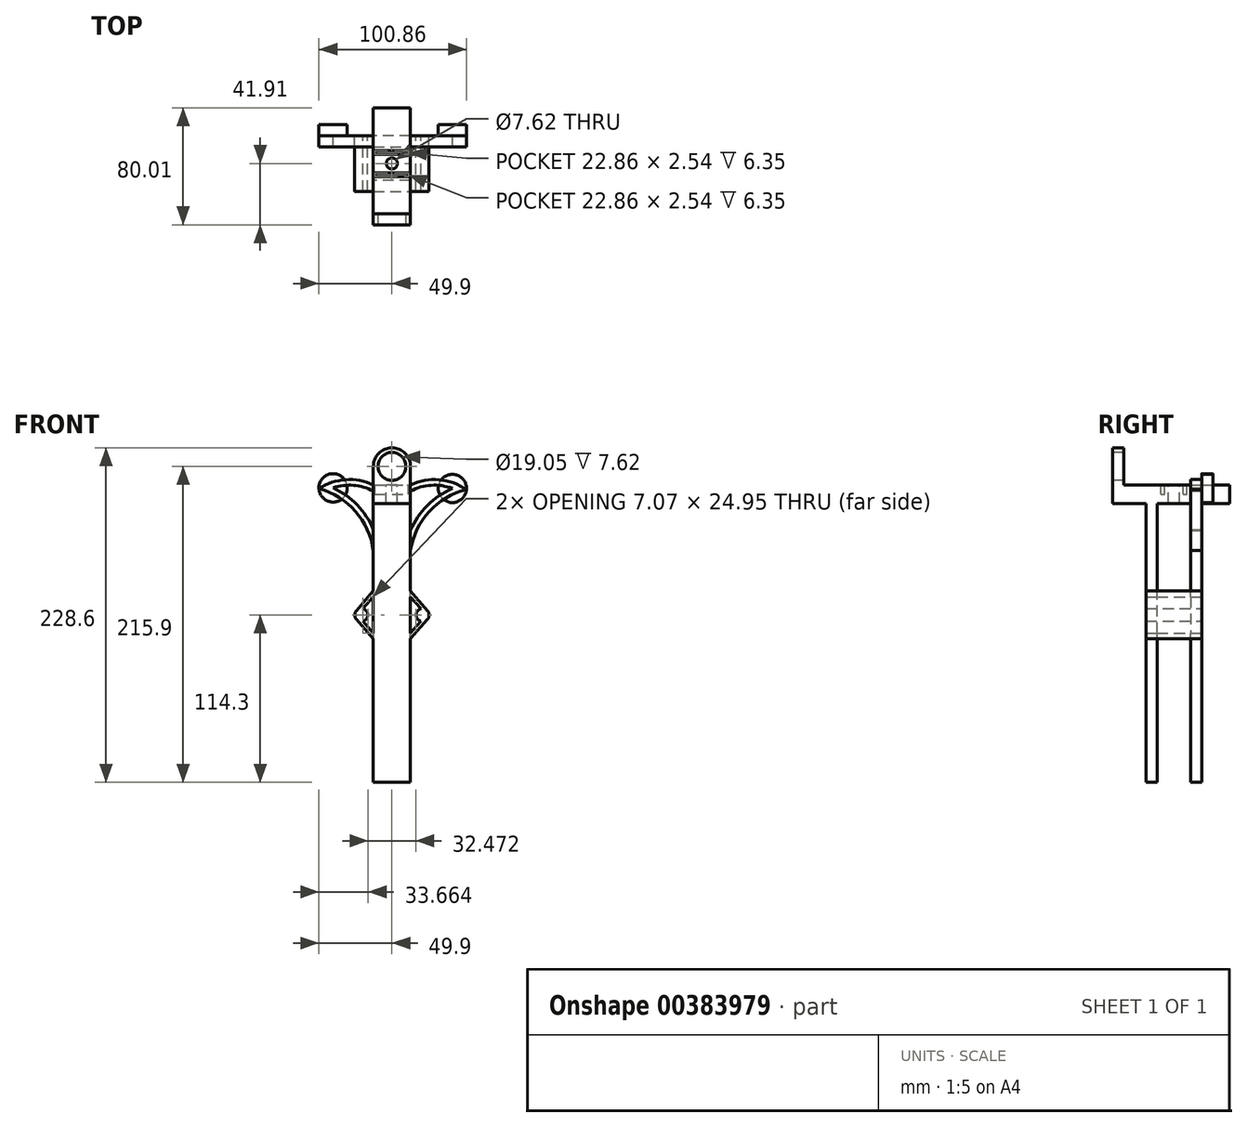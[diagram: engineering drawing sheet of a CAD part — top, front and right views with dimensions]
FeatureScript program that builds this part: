
annotation { "Feature Type Name" : "Feature", "Feature Type Description" : "" }
export const myFeature = defineFeature(function(context is Context, id is Id, definition is map)
    precondition{}
    {
        {
            var Q0;
            Q0=qCreatedBy(makeId("Front.planeOp"),FACE);
            var sketch = newSketch(context, id + "F0", { "sketchPlane" : qUnion([Q0])});
            skLineSegment(sketch, "E0", {"start": v(0, -63.5) * mm, "end": v(0, 139.7) * mm});
            skLineSegment(sketch, "E1", {"start": v(0, 139.7) * mm, "end": v(12.7, 139.7) * mm});
            skLineSegment(sketch, "E2", {"start": v(0, 139.7) * mm, "end": v(-12.7, 139.7) * mm});
            skLineSegment(sketch, "E3", {"start": v(-12.7, 139.7) * mm, "end": v(-12.7, -63.5) * mm});
            skLineSegment(sketch, "E4", {"start": v(-12.7, -63.5) * mm, "end": v(12.7, -63.5) * mm});
            skLineSegment(sketch, "E5", {"start": v(12.7, -63.5) * mm, "end": v(12.7, 139.7) * mm});
            skLineSegment(sketch, "E6", {"start": v(-25.4, 50.8) * mm, "end": v(25.4, 50.8) * mm});
            skArc(sketch, "E7", {"start": v(-24.32, 53.7) * mm, "mid": v(-25.4, 50.8) * mm, "end": v(-24.32, 47.9) * mm});
            skArc(sketch, "E8", {"start": v(24.32, 47.9) * mm, "mid": v(25.4, 50.8) * mm, "end": v(24.32, 53.7) * mm});
            skLineSegment(sketch, "E9", {"start": v(-24.32, 53.7) * mm, "end": v(-12.7, 67.16) * mm});
            skLineSegment(sketch, "E10", {"start": v(-24.32, 47.9) * mm, "end": v(-12.7, 34.44) * mm});
            skLineSegment(sketch, "E11", {"start": v(12.7, 67.16) * mm, "end": v(24.32, 53.7) * mm});
            skLineSegment(sketch, "E12", {"start": v(12.7, 34.44) * mm, "end": v(24.32, 47.9) * mm});
            skLineSegment(sketch, "E13.0", {"start": v(-19.77, 46.52) * mm, "end": v(-12.7, 38.32) * mm});
            skLineSegment(sketch, "E14.0", {"start": v(12.7, 38.32) * mm, "end": v(19.77, 46.52) * mm});
            skLineSegment(sketch, "E15.0", {"start": v(-19.77, 55.08) * mm, "end": v(-12.7, 63.28) * mm});
            skLineSegment(sketch, "E16.0", {"start": v(12.7, 63.28) * mm, "end": v(19.77, 55.08) * mm});
            skArc(sketch, "E17.trimOffspring", {"start": v(-19.77, 46.52) * mm, "mid": v(-16.51, 50.8) * mm, "end": v(-19.77, 55.08) * mm});
            skArc(sketch, "E18.trimOffspring", {"start": v(19.77, 55.08) * mm, "mid": v(16.5, 50.8) * mm, "end": v(19.77, 46.52) * mm});
            skPoint(sketch, "E19.orphan", {"position": v(25.4, 52.45) * mm});
            skSolve(sketch);
        }
        {
            var Q0;
            Q0 = qSketchRegion(id + "F0", true);
            extrude(context, id + "F1", {"entities" : qUnion([Q0]), "endBound" : BoundingType.SYMMETRIC, "depth" : 38.1 * mm});
        }
        {
            var Q0;
            Q0=makeQuery(id+"F1.opExtrude","SWEPT_FACE",FACE,{"disambiguationData":[OSD([sQuery(id+"F0.wireOp",EDGE,"E1"),sQuery(id+"F0.wireOp",EDGE,"E2")])]});
            var Q1;
            Q1=makeQuery(id+"F1.opExtrude","SWEPT_FACE",FACE,{"disambiguationData":[OSD([sQuery(id+"F0.wireOp",EDGE,"E11")])]});
            var Q2;
            {var subQ0=sQuery(id+"F0.wireOp",EDGE,"E5");Q2=makeQuery(id+"F1.opExtrude","SWEPT_FACE",FACE,{"disambiguationData":[OSD([subQ0]),TDD([makeQuery(id+"F0.imprint","IMPRINT",EDGE,{"disambiguationData":[TD([[makeQuery(id+"F0.imprint","INTERSECT",VERTEX,{"derivedFrom":[sQuery(id+"F0.wireOp",EDGE,"E1"),subQ0]}),1.0]])],"derivedFrom":subQ0})])]});}
            var Q3;
            {var subQ0=sQuery(id+"F0.wireOp",EDGE,"E5");Q3=makeQuery(id+"F1.opExtrude","SWEPT_FACE",FACE,{"disambiguationData":[OSD([subQ0]),TDD([makeQuery(id+"F0.imprint","IMPRINT",EDGE,{"disambiguationData":[TD([[makeQuery(id+"F0.imprint","INTERSECT",VERTEX,{"derivedFrom":[subQ0,sQuery(id+"F0.wireOp",EDGE,"E14.0")]}),-1.0]])],"derivedFrom":subQ0}),makeQuery(id+"F0.imprint","IMPRINT",EDGE,{"disambiguationData":[TD([[makeQuery(id+"F0.imprint","INTERSECT",VERTEX,{"derivedFrom":[subQ0,sQuery(id+"F0.wireOp",EDGE,"E16.0")]}),1.0]])],"derivedFrom":subQ0})])]});}
            var Q4;
            Q4=makeQuery(id+"F1.opExtrude","SWEPT_FACE",FACE,{"disambiguationData":[OSD([sQuery(id+"F0.wireOp",EDGE,"E12")])]});
            var Q5;
            {var subQ0=sQuery(id+"F0.wireOp",EDGE,"E5");Q5=makeQuery(id+"F1.opExtrude","SWEPT_FACE",FACE,{"disambiguationData":[OSD([subQ0]),TDD([makeQuery(id+"F0.imprint","IMPRINT",EDGE,{"disambiguationData":[TD([[makeQuery(id+"F0.imprint","INTERSECT",VERTEX,{"derivedFrom":[sQuery(id+"F0.wireOp",EDGE,"E4"),subQ0]}),-1.0]])],"derivedFrom":subQ0})])]});}
            var Q6;
            Q6=makeQuery(id+"F1.opExtrude","SWEPT_FACE",FACE,{"disambiguationData":[OSD([sQuery(id+"F0.wireOp",EDGE,"E4")])]});
            var Q7;
            {var subQ0=sQuery(id+"F0.wireOp",EDGE,"E3");Q7=makeQuery(id+"F1.opExtrude","SWEPT_FACE",FACE,{"disambiguationData":[OSD([subQ0]),TDD([makeQuery(id+"F0.imprint","IMPRINT",EDGE,{"disambiguationData":[TD([[makeQuery(id+"F0.imprint","INTERSECT",VERTEX,{"derivedFrom":[subQ0,sQuery(id+"F0.wireOp",EDGE,"E4")]}),1.0]])],"derivedFrom":subQ0})])]});}
            var Q8;
            Q8=makeQuery(id+"F1.opExtrude","SWEPT_FACE",FACE,{"disambiguationData":[OSD([sQuery(id+"F0.wireOp",EDGE,"E10")])]});
            var Q9;
            Q9=makeQuery(id+"F1.opExtrude","SWEPT_FACE",FACE,{"disambiguationData":[OSD([sQuery(id+"F0.wireOp",EDGE,"E9")])]});
            var Q10;
            {var subQ0=sQuery(id+"F0.wireOp",EDGE,"E3");Q10=makeQuery(id+"F1.opExtrude","SWEPT_FACE",FACE,{"disambiguationData":[OSD([subQ0]),TDD([makeQuery(id+"F0.imprint","IMPRINT",EDGE,{"disambiguationData":[TD([[makeQuery(id+"F0.imprint","INTERSECT",VERTEX,{"derivedFrom":[sQuery(id+"F0.wireOp",EDGE,"E2"),subQ0]}),-1.0]])],"derivedFrom":subQ0})])]});}
            var Q11;
            {var subQ0=sQuery(id+"F0.wireOp",EDGE,"E3");Q11=makeQuery(id+"F1.opExtrude","SWEPT_FACE",FACE,{"disambiguationData":[OSD([subQ0]),TDD([makeQuery(id+"F0.imprint","IMPRINT",EDGE,{"disambiguationData":[TD([[makeQuery(id+"F0.imprint","INTERSECT",VERTEX,{"derivedFrom":[subQ0,sQuery(id+"F0.wireOp",EDGE,"E15.0")]}),-1.0]])],"derivedFrom":subQ0}),makeQuery(id+"F0.imprint","IMPRINT",EDGE,{"disambiguationData":[TD([[makeQuery(id+"F0.imprint","INTERSECT",VERTEX,{"derivedFrom":[subQ0,sQuery(id+"F0.wireOp",EDGE,"E13.0")]}),1.0]])],"derivedFrom":subQ0})])]});}
            var Q12;
            Q12=makeQuery(id+"F1.opExtrude","SWEPT_BODY",BODY,{"disambiguationData":[OSD([sQuery(id+"F0.wireOp",EDGE,"E1"),sQuery(id+"F0.wireOp",EDGE,"E2"),sQuery(id+"F0.wireOp",EDGE,"E3"),sQuery(id+"F0.wireOp",EDGE,"E4"),sQuery(id+"F0.wireOp",EDGE,"E5"),sQuery(id+"F0.wireOp",EDGE,"E7"),sQuery(id+"F0.wireOp",EDGE,"E8"),sQuery(id+"F0.wireOp",EDGE,"E9"),sQuery(id+"F0.wireOp",EDGE,"E10"),sQuery(id+"F0.wireOp",EDGE,"E11"),sQuery(id+"F0.wireOp",EDGE,"E12"),sQuery(id+"F0.wireOp",EDGE,"E13.0"),sQuery(id+"F0.wireOp",EDGE,"E14.0"),sQuery(id+"F0.wireOp",EDGE,"E15.0"),sQuery(id+"F0.wireOp",EDGE,"E16.0"),sQuery(id+"F0.wireOp",EDGE,"E17.trimOffspring"),sQuery(id+"F0.wireOp",EDGE,"E18.trimOffspring")])]});
            shell(context, id + "F2", {"entities" : qUnion([Q0, Q1, Q2, Q3, Q4, Q5, Q6, Q7, Q8, Q9, Q10, Q11]), "parts" : qUnion([Q12]), "thickness" : 7.62 * mm});
        }
        {
            var Q0;
            Q0=makeQuery(id+"F1.opExtrude","CAP_FACE",FACE,{"disambiguationData":[OSD([sQuery(id+"F0.wireOp",EDGE,"E1"),sQuery(id+"F0.wireOp",EDGE,"E2"),sQuery(id+"F0.wireOp",EDGE,"E3"),sQuery(id+"F0.wireOp",EDGE,"E4"),sQuery(id+"F0.wireOp",EDGE,"E5"),sQuery(id+"F0.wireOp",EDGE,"E7"),sQuery(id+"F0.wireOp",EDGE,"E8"),sQuery(id+"F0.wireOp",EDGE,"E9"),sQuery(id+"F0.wireOp",EDGE,"E10"),sQuery(id+"F0.wireOp",EDGE,"E11"),sQuery(id+"F0.wireOp",EDGE,"E12"),sQuery(id+"F0.wireOp",EDGE,"E13.0"),sQuery(id+"F0.wireOp",EDGE,"E14.0"),sQuery(id+"F0.wireOp",EDGE,"E15.0"),sQuery(id+"F0.wireOp",EDGE,"E16.0"),sQuery(id+"F0.wireOp",EDGE,"E17.trimOffspring"),sQuery(id+"F0.wireOp",EDGE,"E18.trimOffspring")])],"isStart":false});
            var sketch = newSketch(context, id + "F3", { "sketchPlane" : qUnion([Q0])});
            skLineSegment(sketch, "E20.bottom", {"start": v(-12.7, 139.7) * mm, "end": v(12.7, 139.7) * mm});
            skLineSegment(sketch, "E20.top", {"start": v(-12.7, 127) * mm, "end": v(12.7, 127) * mm});
            skLineSegment(sketch, "E20.left", {"start": v(-12.7, 139.7) * mm, "end": v(-12.7, 127) * mm});
            skLineSegment(sketch, "E20.right", {"start": v(12.7, 139.7) * mm, "end": v(12.7, 127) * mm});
            skSolve(sketch);
        }
        {
            var Q0;
            Q0=makeQuery(id+"F3.imprint","IMPRINT",FACE,{"disambiguationData":[TD([[makeQuery(id+"F3.imprint","IMPRINT",EDGE,{"derivedFrom":sQuery(id+"F3.wireOp",EDGE,"E20.bottom")}),-1.0]])]});
            extrude(context, id + "F4", {"entities" : qUnion([Q0]), "operationType" : NewBodyOperationType.ADD, "depth" : 22.86 * mm});
        }
        {
            var Q0;
            Q0=makeQuery(id+"F4.opExtrude","CAP_FACE",FACE,{"disambiguationData":[OSD([sQuery(id+"F3.wireOp",EDGE,"E20.bottom"),sQuery(id+"F3.wireOp",EDGE,"E20.top"),sQuery(id+"F3.wireOp",EDGE,"E20.left"),sQuery(id+"F3.wireOp",EDGE,"E20.right")])],"isStart":false});
            var sketch = newSketch(context, id + "F5", { "sketchPlane" : qUnion([Q0])});
            skCircle(sketch, "E21", {"center": v(0, 152.4) * mm, "radius": 12.7 * mm});
            skLineSegment(sketch, "E22", {"start": v(-12.7, 127) * mm, "end": v(-12.7, 152.4) * mm});
            skLineSegment(sketch, "E23", {"start": v(12.7, 127) * mm, "end": v(12.7, 152.4) * mm});
            skCircle(sketch, "E24", {"center": v(0, 152.4) * mm, "radius": 9.53 * mm});
            skSolve(sketch);
        }
        {
            var Q0;
            Q0=makeQuery(id+"F5.imprint","IMPRINT",FACE,{"disambiguationData":[TD([[makeQuery(id+"F5.imprint","IMPRINT",EDGE,{"derivedFrom":sQuery(id+"F5.wireOp",EDGE,"E24")}),-1.0]])]});
            var Q1;
            {var subQ0=sQuery(id+"F5.wireOp",EDGE,"E22");var subQ1=sQuery(id+"F5.wireOp",EDGE,"E21");var subQ2=makeQuery(id+"F5.imprint","INTERSECT",VERTEX,{"derivedFrom":[subQ1,subQ0]});Q1=makeQuery(id+"F5.imprint","IMPRINT",FACE,{"disambiguationData":[TD([[makeQuery(id+"F5.imprint","IMPRINT",EDGE,{"disambiguationData":[TD([[subQ2,-1.0]])],"derivedFrom":subQ1}),-1.0]])]});}
            var Q2;
            {var subQ0=sQuery(id+"F5.wireOp",EDGE,"E23");var subQ1=sQuery(id+"F5.wireOp",EDGE,"E21");var subQ2=makeQuery(id+"F5.imprint","INTERSECT",VERTEX,{"derivedFrom":[subQ1,subQ0]});Q2=makeQuery(id+"F5.imprint","IMPRINT",FACE,{"disambiguationData":[TD([[makeQuery(id+"F5.imprint","IMPRINT",EDGE,{"disambiguationData":[TD([[subQ2,1.0]])],"derivedFrom":subQ1}),-1.0]])]});}
            extrude(context, id + "F6", {"entities" : qUnion([Q0, Q1, Q2]), "operationType" : NewBodyOperationType.ADD, "oppositeDirection" : true, "depth" : 7.62 * mm});
        }
        {
            var Q0;
            Q0=makeQuery(id+"F1.opExtrude","CAP_FACE",FACE,{"disambiguationData":[OSD([sQuery(id+"F0.wireOp",EDGE,"E1"),sQuery(id+"F0.wireOp",EDGE,"E2"),sQuery(id+"F0.wireOp",EDGE,"E3"),sQuery(id+"F0.wireOp",EDGE,"E4"),sQuery(id+"F0.wireOp",EDGE,"E5"),sQuery(id+"F0.wireOp",EDGE,"E7"),sQuery(id+"F0.wireOp",EDGE,"E8"),sQuery(id+"F0.wireOp",EDGE,"E9"),sQuery(id+"F0.wireOp",EDGE,"E10"),sQuery(id+"F0.wireOp",EDGE,"E11"),sQuery(id+"F0.wireOp",EDGE,"E12"),sQuery(id+"F0.wireOp",EDGE,"E13.0"),sQuery(id+"F0.wireOp",EDGE,"E14.0"),sQuery(id+"F0.wireOp",EDGE,"E15.0"),sQuery(id+"F0.wireOp",EDGE,"E16.0"),sQuery(id+"F0.wireOp",EDGE,"E17.trimOffspring"),sQuery(id+"F0.wireOp",EDGE,"E18.trimOffspring")])],"isStart":true});
            var sketch = newSketch(context, id + "F7", { "sketchPlane" : qUnion([Q0])});
            skLineSegment(sketch, "E25.bottom", {"start": v(-12.7, 139.7) * mm, "end": v(12.7, 139.7) * mm});
            skLineSegment(sketch, "E25.top", {"start": v(-12.7, 127) * mm, "end": v(12.7, 127) * mm});
            skLineSegment(sketch, "E25.left", {"start": v(-12.7, 139.7) * mm, "end": v(-12.7, 127) * mm});
            skLineSegment(sketch, "E25.right", {"start": v(12.7, 139.7) * mm, "end": v(12.7, 127) * mm});
            skSolve(sketch);
        }
        {
            var Q0;
            Q0=makeQuery(id+"F7.imprint","IMPRINT",FACE,{"disambiguationData":[TD([[makeQuery(id+"F7.imprint","IMPRINT",EDGE,{"derivedFrom":sQuery(id+"F7.wireOp",EDGE,"E25.bottom")}),1.0]])]});
            var Q1;
            {var subQ0=sQuery(id+"F0.wireOp",EDGE,"E18.trimOffspring");var subQ1=sQuery(id+"F0.wireOp",EDGE,"E17.trimOffspring");var subQ2=sQuery(id+"F0.wireOp",EDGE,"E16.0");var subQ3=sQuery(id+"F0.wireOp",EDGE,"E15.0");var subQ4=sQuery(id+"F0.wireOp",EDGE,"E14.0");var subQ5=sQuery(id+"F0.wireOp",EDGE,"E13.0");var subQ6=sQuery(id+"F0.wireOp",EDGE,"E12");var subQ7=sQuery(id+"F0.wireOp",EDGE,"E11");var subQ8=sQuery(id+"F0.wireOp",EDGE,"E10");var subQ9=sQuery(id+"F0.wireOp",EDGE,"E9");var subQ10=sQuery(id+"F0.wireOp",EDGE,"E8");var subQ11=sQuery(id+"F0.wireOp",EDGE,"E7");var subQ12=sQuery(id+"F0.wireOp",EDGE,"E5");var subQ13=sQuery(id+"F0.wireOp",EDGE,"E4");var subQ14=sQuery(id+"F0.wireOp",EDGE,"E3");var subQ15=sQuery(id+"F0.wireOp",EDGE,"E2");var subQ16=sQuery(id+"F0.wireOp",EDGE,"E1");Q1=makeQuery(id+"F2.opShell","OFFSET_FACE",FACE,{"disambiguationData":[OSD([subQ16,subQ15,subQ14,subQ13,subQ12,subQ11,subQ10,subQ9,subQ8,subQ7,subQ6,subQ5,subQ4,subQ3,subQ2,subQ1,subQ0]),TDD([makeQuery(id+"F1.opExtrude","CAP_FACE",FACE,{"disambiguationData":[OSD([subQ16,subQ15,subQ14,subQ13,subQ12,subQ11,subQ10,subQ9,subQ8,subQ7,subQ6,subQ5,subQ4,subQ3,subQ2,subQ1,subQ0])],"isStart":false})])]});}
            extrude(context, id + "F8", {"entities" : qUnion([Q0]), "operationType" : NewBodyOperationType.ADD, "endBound" : BoundingType.UP_TO_SURFACE, "oppositeDirection" : true, "endBoundEntityFace" : qUnion([Q1]), "depth" : 25.4 * mm});
        }
        {
            var Q0;
            Q0=makeQuery(id+"F1.opExtrude","CAP_FACE",FACE,{"disambiguationData":[OSD([sQuery(id+"F0.wireOp",EDGE,"E1"),sQuery(id+"F0.wireOp",EDGE,"E2"),sQuery(id+"F0.wireOp",EDGE,"E3"),sQuery(id+"F0.wireOp",EDGE,"E4"),sQuery(id+"F0.wireOp",EDGE,"E5"),sQuery(id+"F0.wireOp",EDGE,"E7"),sQuery(id+"F0.wireOp",EDGE,"E8"),sQuery(id+"F0.wireOp",EDGE,"E9"),sQuery(id+"F0.wireOp",EDGE,"E10"),sQuery(id+"F0.wireOp",EDGE,"E11"),sQuery(id+"F0.wireOp",EDGE,"E12"),sQuery(id+"F0.wireOp",EDGE,"E13.0"),sQuery(id+"F0.wireOp",EDGE,"E14.0"),sQuery(id+"F0.wireOp",EDGE,"E15.0"),sQuery(id+"F0.wireOp",EDGE,"E16.0"),sQuery(id+"F0.wireOp",EDGE,"E17.trimOffspring"),sQuery(id+"F0.wireOp",EDGE,"E18.trimOffspring")])],"isStart":true});
            var sketch = newSketch(context, id + "F9", { "sketchPlane" : qUnion([Q0])});
            skLineSegment(sketch, "E26.bottom", {"start": v(-12.7, 139.7) * mm, "end": v(12.7, 139.7) * mm});
            skLineSegment(sketch, "E26.top", {"start": v(-12.7, 127) * mm, "end": v(12.7, 127) * mm});
            skLineSegment(sketch, "E26.left", {"start": v(-12.7, 139.7) * mm, "end": v(-12.7, 127) * mm});
            skLineSegment(sketch, "E26.right", {"start": v(12.7, 139.7) * mm, "end": v(12.7, 127) * mm});
            skSolve(sketch);
        }
        {
            var Q0;
            Q0=makeQuery(id+"F9.imprint","IMPRINT",FACE,{"disambiguationData":[TD([[makeQuery(id+"F9.imprint","IMPRINT",EDGE,{"derivedFrom":sQuery(id+"F9.wireOp",EDGE,"E26.bottom")}),1.0]])]});
            extrude(context, id + "F10", {"entities" : qUnion([Q0]), "operationType" : NewBodyOperationType.ADD, "depth" : 19.05 * mm});
        }
        {
            var Q0;
            Q0=makeQuery(id+"F1.opExtrude","CAP_FACE",FACE,{"disambiguationData":[OSD([sQuery(id+"F0.wireOp",EDGE,"E1"),sQuery(id+"F0.wireOp",EDGE,"E2"),sQuery(id+"F0.wireOp",EDGE,"E3"),sQuery(id+"F0.wireOp",EDGE,"E4"),sQuery(id+"F0.wireOp",EDGE,"E5"),sQuery(id+"F0.wireOp",EDGE,"E7"),sQuery(id+"F0.wireOp",EDGE,"E8"),sQuery(id+"F0.wireOp",EDGE,"E9"),sQuery(id+"F0.wireOp",EDGE,"E10"),sQuery(id+"F0.wireOp",EDGE,"E11"),sQuery(id+"F0.wireOp",EDGE,"E12"),sQuery(id+"F0.wireOp",EDGE,"E13.0"),sQuery(id+"F0.wireOp",EDGE,"E14.0"),sQuery(id+"F0.wireOp",EDGE,"E15.0"),sQuery(id+"F0.wireOp",EDGE,"E16.0"),sQuery(id+"F0.wireOp",EDGE,"E17.trimOffspring"),sQuery(id+"F0.wireOp",EDGE,"E18.trimOffspring")])],"isStart":true});
            var sketch = newSketch(context, id + "F11", { "sketchPlane" : qUnion([Q0])});
            skLineSegment(sketch, "E27.0.0", {"start": v(-12.7, 139.7) * mm, "end": v(-12.7, 127) * mm});
            skLineSegment(sketch, "E27.0.1", {"start": v(-12.7, 127) * mm, "end": v(12.7, 127) * mm});
            skLineSegment(sketch, "E27.0.2", {"start": v(12.7, 127) * mm, "end": v(12.7, 139.7) * mm});
            skLineSegment(sketch, "E27.0.3", {"start": v(12.7, 139.7) * mm, "end": v(-12.7, 139.7) * mm});
            skArc(sketch, "E28", {"start": v(49.88, 137.18) * mm, "mid": v(31.62, 143.3) * mm, "end": v(12.7, 139.7) * mm});
            skArc(sketch, "E29", {"start": v(-12.7, 94.77) * mm, "mid": v(-25.42, 121.48) * mm, "end": v(-50.92, 136.48) * mm});
            skArc(sketch, "E30", {"start": v(12.7, 94.77) * mm, "mid": v(24.86, 121.61) * mm, "end": v(49.88, 137.18) * mm});
            skArc(sketch, "E31.trimOffspring", {"start": v(-12.7, 139.7) * mm, "mid": v(-32.24, 143.25) * mm, "end": v(-50.92, 136.48) * mm});
            skArc(sketch, "E32.0", {"start": v(-12.7, 135.43) * mm, "mid": v(-26.8, 139.5) * mm, "end": v(-41.32, 137.3) * mm});
            skArc(sketch, "E33.0", {"start": v(-12.7, 108.67) * mm, "mid": v(-24.24, 125.75) * mm, "end": v(-41.32, 137.3) * mm});
            skArc(sketch, "E34.0", {"start": v(12.7, 109.24) * mm, "mid": v(23.77, 126.05) * mm, "end": v(40.2, 137.71) * mm});
            skArc(sketch, "E35.trimOffspring", {"start": v(40.2, 137.71) * mm, "mid": v(26.2, 139.46) * mm, "end": v(12.7, 135.43) * mm});
            skLineSegment(sketch, "E36.0.0", {"start": v(12.7, 127) * mm, "end": v(-12.7, 127) * mm});
            skLineSegment(sketch, "E36.0.1", {"start": v(-12.7, 127) * mm, "end": v(-12.7, 67.16) * mm});
            skLineSegment(sketch, "E36.0.2", {"start": v(-12.7, 67.16) * mm, "end": v(-24.32, 53.7) * mm});
            skArc(sketch, "E36.0.3", {"start": v(-24.32, 53.7) * mm, "mid": v(-25.4, 50.8) * mm, "end": v(-24.32, 47.9) * mm});
            skLineSegment(sketch, "E36.0.4", {"start": v(-24.32, 47.9) * mm, "end": v(-12.7, 34.44) * mm});
            skLineSegment(sketch, "E36.0.5", {"start": v(-12.7, 34.44) * mm, "end": v(-12.7, -63.5) * mm});
            skLineSegment(sketch, "E36.0.6", {"start": v(-12.7, -63.5) * mm, "end": v(12.7, -63.5) * mm});
            skLineSegment(sketch, "E36.0.7", {"start": v(12.7, -63.5) * mm, "end": v(12.7, 34.44) * mm});
            skLineSegment(sketch, "E36.0.8", {"start": v(12.7, 34.44) * mm, "end": v(24.32, 47.9) * mm});
            skArc(sketch, "E36.0.9", {"start": v(24.32, 47.9) * mm, "mid": v(25.4, 50.8) * mm, "end": v(24.32, 53.7) * mm});
            skLineSegment(sketch, "E36.0.10", {"start": v(24.32, 53.7) * mm, "end": v(12.7, 67.16) * mm});
            skLineSegment(sketch, "E36.0.11", {"start": v(12.7, 67.16) * mm, "end": v(12.7, 127) * mm});
            skSolve(sketch);
        }
        {
            var Q0;
            {var subQ2=sQuery(id+"F11.wireOp",EDGE,"E29");Q0=makeQuery(id+"F11.imprint","IMPRINT",FACE,{"disambiguationData":[TD([[makeQuery(id+"F11.imprint","IMPRINT",EDGE,{"derivedFrom":subQ2}),-1.0]])]});}
            var Q1;
            {var subQ2=sQuery(id+"F11.wireOp",EDGE,"E28");Q1=makeQuery(id+"F11.imprint","IMPRINT",FACE,{"disambiguationData":[TD([[makeQuery(id+"F11.imprint","IMPRINT",EDGE,{"derivedFrom":subQ2}),1.0]])]});}
            extrude(context, id + "F12", {"entities" : qUnion([Q0, Q1]), "operationType" : NewBodyOperationType.ADD, "oppositeDirection" : true, "depth" : 7.62 * mm});
        }
        {
            var Q0;
            Q0=makeQuery(id+"F12.boolean.opBoolean","MERGE",FACE,{"derivedFrom":[makeQuery(id+"F1.opExtrude","CAP_FACE",FACE,{"disambiguationData":[OSD([sQuery(id+"F0.wireOp",EDGE,"E1"),sQuery(id+"F0.wireOp",EDGE,"E2"),sQuery(id+"F0.wireOp",EDGE,"E3"),sQuery(id+"F0.wireOp",EDGE,"E4"),sQuery(id+"F0.wireOp",EDGE,"E5"),sQuery(id+"F0.wireOp",EDGE,"E7"),sQuery(id+"F0.wireOp",EDGE,"E8"),sQuery(id+"F0.wireOp",EDGE,"E9"),sQuery(id+"F0.wireOp",EDGE,"E10"),sQuery(id+"F0.wireOp",EDGE,"E11"),sQuery(id+"F0.wireOp",EDGE,"E12"),sQuery(id+"F0.wireOp",EDGE,"E13.0"),sQuery(id+"F0.wireOp",EDGE,"E14.0"),sQuery(id+"F0.wireOp",EDGE,"E15.0"),sQuery(id+"F0.wireOp",EDGE,"E16.0"),sQuery(id+"F0.wireOp",EDGE,"E17.trimOffspring"),sQuery(id+"F0.wireOp",EDGE,"E18.trimOffspring")])],"isStart":true}),makeQuery(id+"F12.opExtrude","CAP_FACE",FACE,{"disambiguationData":[OSD([sQuery(id+"F11.wireOp",EDGE,"E27.0.0"),sQuery(id+"F11.wireOp",EDGE,"E29"),sQuery(id+"F11.wireOp",EDGE,"E31.trimOffspring"),sQuery(id+"F11.wireOp",EDGE,"E32.0"),sQuery(id+"F11.wireOp",EDGE,"E33.0"),sQuery(id+"F11.wireOp",EDGE,"E36.0.1")])],"isStart":true}),makeQuery(id+"F12.opExtrude","CAP_FACE",FACE,{"disambiguationData":[OSD([sQuery(id+"F11.wireOp",EDGE,"E27.0.2"),sQuery(id+"F11.wireOp",EDGE,"E28"),sQuery(id+"F11.wireOp",EDGE,"E30"),sQuery(id+"F11.wireOp",EDGE,"E34.0"),sQuery(id+"F11.wireOp",EDGE,"E35.trimOffspring"),sQuery(id+"F11.wireOp",EDGE,"E36.0.11")])],"isStart":true})]});
            var sketch = newSketch(context, id + "F13", { "sketchPlane" : qUnion([Q0])});
            skCircle(sketch, "E37", {"center": v(-41.32, 137.3) * mm, "radius": 9.64 * mm});
            skCircle(sketch, "E38", {"center": v(40.2, 137.71) * mm, "radius": 9.7 * mm});
            skSolve(sketch);
        }
        {
            var Q0;
            Q0 = qSketchRegion(id + "F13", true);
            extrude(context, id + "F14", {"entities" : qUnion([Q0]), "operationType" : NewBodyOperationType.ADD, "depth" : 7.62 * mm});
        }
        {
            var Q0;
            {var subQ0=sQuery(id+"F0.wireOp",EDGE,"E2");var subQ1=sQuery(id+"F0.wireOp",EDGE,"E1");Q0=makeQuery(id+"F10.boolean.opBoolean","MERGE",FACE,{"derivedFrom":[makeQuery(id+"F8.boolean.opBoolean","MERGE",FACE,{"derivedFrom":[makeQuery(id+"F2.opShell","OFFSET_FACE",FACE,{"disambiguationData":[OSD([subQ1,subQ0])]}),makeQuery(id+"F4.boolean.opBoolean","MERGE",FACE,{"derivedFrom":[makeQuery(id+"F1.opExtrude","SWEPT_FACE",FACE,{"disambiguationData":[OSD([subQ1,subQ0])]}),makeQuery(id+"F4.opExtrude","SWEPT_FACE",FACE,{"disambiguationData":[OSD([sQuery(id+"F3.wireOp",EDGE,"E20.bottom")])]})]}),makeQuery(id+"F8.opExtrude","SWEPT_FACE",FACE,{"disambiguationData":[OSD([sQuery(id+"F7.wireOp",EDGE,"E25.bottom")])]})]}),makeQuery(id+"F10.opExtrude","SWEPT_FACE",FACE,{"disambiguationData":[OSD([sQuery(id+"F9.wireOp",EDGE,"E26.bottom")])]})]});}
            var sketch = newSketch(context, id + "F15", { "sketchPlane" : qUnion([Q0])});
            skLineSegment(sketch, "E39.bottom", {"start": v(-12.7, -10.16) * mm, "end": v(12.7, -10.16) * mm});
            skLineSegment(sketch, "E39.top", {"start": v(-12.7, -5.08) * mm, "end": v(12.7, -5.08) * mm});
            skLineSegment(sketch, "E39.left", {"start": v(-12.7, -10.16) * mm, "end": v(-12.7, -5.08) * mm});
            skLineSegment(sketch, "E39.right", {"start": v(12.7, -10.16) * mm, "end": v(12.7, -5.08) * mm});
            skLineSegment(sketch, "E40.bottom", {"start": v(-12.7, 5.08) * mm, "end": v(12.7, 5.08) * mm});
            skLineSegment(sketch, "E40.top", {"start": v(-12.7, 10.16) * mm, "end": v(12.7, 10.16) * mm});
            skLineSegment(sketch, "E40.left", {"start": v(-12.7, 5.08) * mm, "end": v(-12.7, 10.16) * mm});
            skLineSegment(sketch, "E40.right", {"start": v(12.7, 5.08) * mm, "end": v(12.7, 10.16) * mm});
            skLineSegment(sketch, "E41.bottom", {"start": v(-11.43, -8.9) * mm, "end": v(11.43, -8.9) * mm});
            skLineSegment(sketch, "E41.top", {"start": v(-11.43, -6.35) * mm, "end": v(11.43, -6.35) * mm});
            skLineSegment(sketch, "E41.left", {"start": v(-11.43, -8.9) * mm, "end": v(-11.43, -6.35) * mm});
            skLineSegment(sketch, "E41.right", {"start": v(11.43, -8.9) * mm, "end": v(11.43, -6.35) * mm});
            skLineSegment(sketch, "E42.bottom", {"start": v(-11.43, 6.35) * mm, "end": v(11.43, 6.35) * mm});
            skLineSegment(sketch, "E42.top", {"start": v(-11.43, 8.9) * mm, "end": v(11.43, 8.9) * mm});
            skLineSegment(sketch, "E42.left", {"start": v(-11.43, 6.35) * mm, "end": v(-11.43, 8.9) * mm});
            skLineSegment(sketch, "E42.right", {"start": v(11.43, 6.35) * mm, "end": v(11.43, 8.9) * mm});
            skSolve(sketch);
        }
        {
            var Q0;
            Q0=makeQuery(id+"F15.imprint","IMPRINT",FACE,{"disambiguationData":[TD([[makeQuery(id+"F15.imprint","IMPRINT",EDGE,{"derivedFrom":sQuery(id+"F15.wireOp",EDGE,"E41.bottom")}),1.0]])]});
            var Q1;
            Q1=makeQuery(id+"F15.imprint","IMPRINT",FACE,{"disambiguationData":[TD([[makeQuery(id+"F15.imprint","IMPRINT",EDGE,{"derivedFrom":sQuery(id+"F15.wireOp",EDGE,"E42.bottom")}),1.0]])]});
            extrude(context, id + "F16", {"entities" : qUnion([Q0, Q1]), "operationType" : NewBodyOperationType.REMOVE, "oppositeDirection" : true, "depth" : 6.35 * mm});
        }
        {
            var Q0;
            {var subQ0=sQuery(id+"F0.wireOp",EDGE,"E2");var subQ1=sQuery(id+"F0.wireOp",EDGE,"E1");Q0=makeQuery(id+"F10.boolean.opBoolean","MERGE",FACE,{"derivedFrom":[makeQuery(id+"F8.boolean.opBoolean","MERGE",FACE,{"derivedFrom":[makeQuery(id+"F2.opShell","OFFSET_FACE",FACE,{"disambiguationData":[OSD([subQ1,subQ0])]}),makeQuery(id+"F4.boolean.opBoolean","MERGE",FACE,{"derivedFrom":[makeQuery(id+"F1.opExtrude","SWEPT_FACE",FACE,{"disambiguationData":[OSD([subQ1,subQ0])]}),makeQuery(id+"F4.opExtrude","SWEPT_FACE",FACE,{"disambiguationData":[OSD([sQuery(id+"F3.wireOp",EDGE,"E20.bottom")])]})]}),makeQuery(id+"F8.opExtrude","SWEPT_FACE",FACE,{"disambiguationData":[OSD([sQuery(id+"F7.wireOp",EDGE,"E25.bottom")])]})]}),makeQuery(id+"F10.opExtrude","SWEPT_FACE",FACE,{"disambiguationData":[OSD([sQuery(id+"F9.wireOp",EDGE,"E26.bottom")])]})]});}
            var sketch = newSketch(context, id + "F17", { "sketchPlane" : qUnion([Q0])});
            skCircle(sketch, "E43", {"center": v(0, 0) * mm, "radius": 3.81 * mm});
            skSolve(sketch);
        }
        {
            var Q0;
            Q0=makeQuery(id+"F17.imprint","IMPRINT",FACE,{"disambiguationData":[TD([[makeQuery(id+"F17.imprint","IMPRINT",EDGE,{"derivedFrom":sQuery(id+"F17.wireOp",EDGE,"E43")}),1.0]])]});
            extrude(context, id + "F18", {"entities" : qUnion([Q0]), "operationType" : NewBodyOperationType.REMOVE, "endBound" : BoundingType.UP_TO_NEXT, "oppositeDirection" : true, "depth" : 25.4 * mm});
        }
    });
